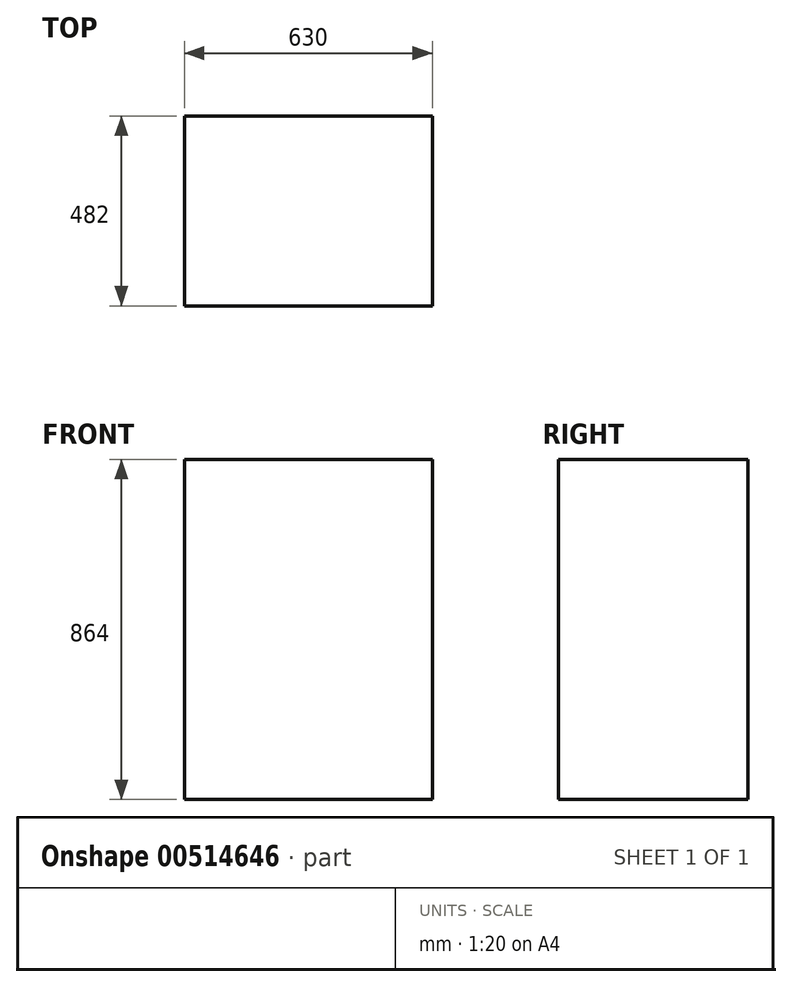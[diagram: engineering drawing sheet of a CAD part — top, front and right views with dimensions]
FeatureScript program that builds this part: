
annotation { "Feature Type Name" : "Feature", "Feature Type Description" : "" }
export const myFeature = defineFeature(function(context is Context, id is Id, definition is map)
    precondition{}
    {
        {
            var Q0;
            Q0=qCreatedBy(makeId("Top.planeOp"),FACE);
            var sketch = newSketch(context, id + "F0", { "sketchPlane" : qUnion([Q0])});
            skLineSegment(sketch, "E0.bottom", {"start": v(-299.93, 191.8) * mm, "end": v(330.07, 191.8) * mm});
            skLineSegment(sketch, "E0.top", {"start": v(-299.93, -290.2) * mm, "end": v(330.07, -290.2) * mm});
            skLineSegment(sketch, "E0.left", {"start": v(-299.93, 191.8) * mm, "end": v(-299.93, -290.2) * mm});
            skLineSegment(sketch, "E0.right", {"start": v(330.07, 191.8) * mm, "end": v(330.07, -290.2) * mm});
            skSolve(sketch);
        }
        {
            var Q0;
            Q0 = qSketchRegion(id + "F0", true);
            extrude(context, id + "F1", {"entities" : qUnion([Q0]), "depth" : 864 * mm, "offsetDistance" : 25.4 * mm});
        }
        {
            var Q0;
            Q0=makeQuery(id+"F1.opExtrude","CAP_FACE",FACE,{"disambiguationData":[OSD([sQuery(id+"F0.wireOp",EDGE,"E0.bottom"),sQuery(id+"F0.wireOp",EDGE,"E0.top"),sQuery(id+"F0.wireOp",EDGE,"E0.left"),sQuery(id+"F0.wireOp",EDGE,"E0.right")])],"isStart":false});
            var sketch = newSketch(context, id + "F2", { "sketchPlane" : qUnion([Q0])});
            skLineSegment(sketch, "E1.0", {"start": v(-267.93, 159.8) * mm, "end": v(-267.93, -258.2) * mm});
            skLineSegment(sketch, "E1.1", {"start": v(298.07, 159.8) * mm, "end": v(-267.93, 159.8) * mm});
            skLineSegment(sketch, "E1.2", {"start": v(298.07, -258.2) * mm, "end": v(298.07, 159.8) * mm});
            skLineSegment(sketch, "E1.3", {"start": v(-267.93, -258.2) * mm, "end": v(298.07, -258.2) * mm});
            skSolve(sketch);
        }
        {
            var Q0;
            Q0 = qConstructionFilter(qBodyType(qCreatedBy(id + "F2" ,EDGE), BodyType.WIRE), ConstructionObject.NO);
            extrude(context, id + "F3", {"bodyType" : ToolBodyType.SURFACE, "surfaceEntities" : qUnion([Q0]), "oppositeDirection" : true, "depth" : 16 * mm, "offsetDistance" : 25.4 * mm});
        }
    });
